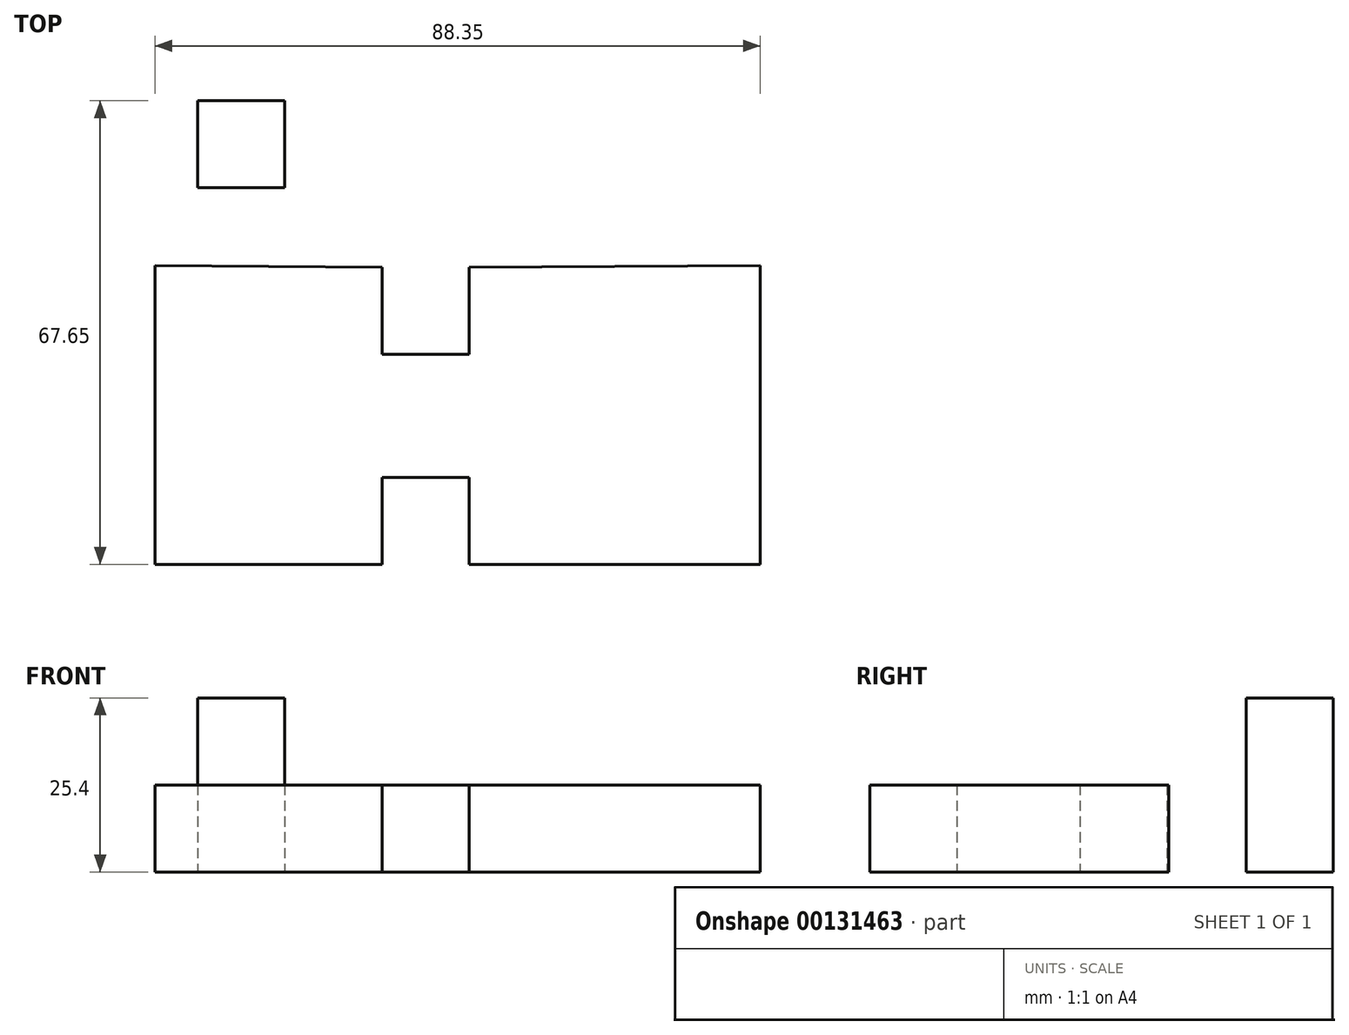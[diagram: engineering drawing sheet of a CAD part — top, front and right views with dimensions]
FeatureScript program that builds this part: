
annotation { "Feature Type Name" : "Feature", "Feature Type Description" : "" }
export const myFeature = defineFeature(function(context is Context, id is Id, definition is map)
    precondition{}
    {
        {
            var Q0;
            Q0=qCreatedBy(makeId("Top.planeOp"),FACE);
            var sketch = newSketch(context, id + "F0", { "sketchPlane" : qUnion([Q0])});
            skLineSegment(sketch, "E0.bottom", {"start": v(-39.63, 19.75) * mm, "end": v(-26.93, 19.75) * mm});
            skLineSegment(sketch, "E0.top", {"start": v(-39.63, 7.05) * mm, "end": v(-26.93, 7.05) * mm});
            skLineSegment(sketch, "E0.left", {"start": v(-39.63, 19.75) * mm, "end": v(-39.63, 7.05) * mm});
            skLineSegment(sketch, "E0.right", {"start": v(-26.93, 19.75) * mm, "end": v(-26.93, 7.05) * mm});
            skSolve(sketch);
        }
        {
            var Q0;
            Q0=makeQuery(id+"F0.imprint","IMPRINT",FACE,{"disambiguationData":[TD([[makeQuery(id+"F0.imprint","IMPRINT",EDGE,{"derivedFrom":sQuery(id+"F0.wireOp",EDGE,"E0.bottom")}),-1.0]])]});
            extrude(context, id + "F1", {"entities" : qUnion([Q0]), "depth" : 25.4 * mm});
        }
        {
            var Q0;
            Q0=qCreatedBy(makeId("Top.planeOp"),FACE);
            var sketch = newSketch(context, id + "F2", { "sketchPlane" : qUnion([Q0])});
            skLineSegment(sketch, "E1.top", {"start": v(-45.83, -47.9) * mm, "end": v(-12.7, -47.9) * mm});
            skLineSegment(sketch, "E1.left", {"start": v(-45.83, -4.28) * mm, "end": v(-45.83, -47.9) * mm});
            skLineSegment(sketch, "E1.right", {"start": v(42.52, -4.28) * mm, "end": v(42.52, -47.9) * mm});
            skLineSegment(sketch, "E2.top", {"start": v(-12.7, -17.26) * mm, "end": v(0, -17.26) * mm});
            skLineSegment(sketch, "E2.left", {"start": v(-12.7, -4.56) * mm, "end": v(-12.7, -17.26) * mm});
            skLineSegment(sketch, "E2.right", {"start": v(0, -4.56) * mm, "end": v(0, -17.26) * mm});
            skLineSegment(sketch, "E3.bottom", {"start": v(-12.7, -35.23) * mm, "end": v(0, -35.23) * mm});
            skLineSegment(sketch, "E3.left", {"start": v(-12.7, -35.23) * mm, "end": v(-12.7, -47.93) * mm});
            skLineSegment(sketch, "E3.right", {"start": v(0, -35.23) * mm, "end": v(0, -47.93) * mm});
            skLineSegment(sketch, "E4.trimOffspring", {"start": v(0, -47.9) * mm, "end": v(42.52, -47.9) * mm});
            skLineSegment(sketch, "E5", {"start": v(-45.83, -4.28) * mm, "end": v(-12.7, -4.56) * mm});
            skLineSegment(sketch, "E6", {"start": v(0, -4.56) * mm, "end": v(42.52, -4.28) * mm});
            skSolve(sketch);
        }
        {
            var Q0;
            {var subQ4=sQuery(id+"F2.wireOp",EDGE,"E1.top");Q0=makeQuery(id+"F2.imprint","IMPRINT",FACE,{"disambiguationData":[TD([[makeQuery(id+"F2.imprint","IMPRINT",EDGE,{"derivedFrom":subQ4}),1.0]])]});}
            extrude(context, id + "F3", {"entities" : qUnion([Q0]), "depth" : 12.7 * mm});
        }
    });
